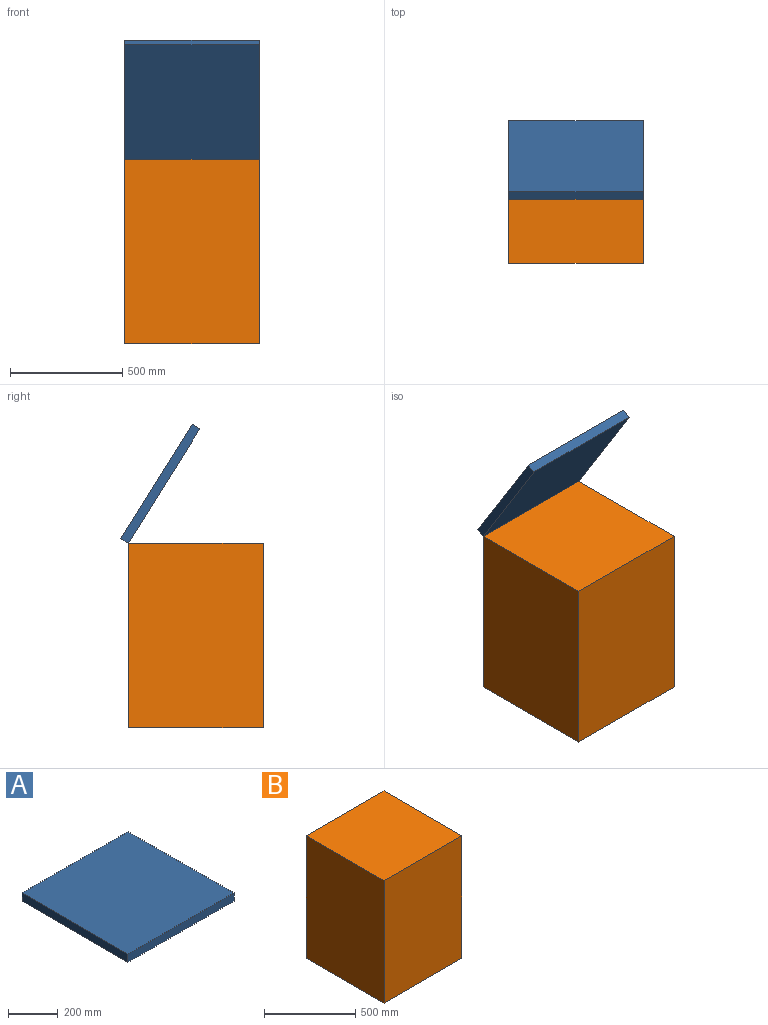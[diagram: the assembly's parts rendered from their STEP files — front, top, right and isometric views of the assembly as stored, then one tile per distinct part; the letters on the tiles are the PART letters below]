
ASSEMBLY  parts=2 mates=1
PART A: 6 faces, bbox 600x600x40 mm
  f0: plane 600x40mm, normal (1,0,0), area 24000mm2, adj f1,f3,f4,f5
  f1: plane 600x40mm, normal (0,1,0), area 24000mm2, adj f0,f2,f4,f5
  f2: plane 600x40mm, normal (-1,0,0), area 24000mm2, adj f1,f3,f4,f5
  f3: plane 600x40mm, normal (0,-1,0), area 24000mm2, adj f0,f2,f4,f5
  f4: plane 600x600mm, normal (0,0,1), area 360000mm2, adj f0,f1,f2,f3
  f5: plane 600x600mm, normal (0,0,-1), area 360000mm2, adj f0,f1,f2,f3
PART B: 6 faces, bbox 600x600x820 mm
  f0: plane 820x600mm, normal (1,0,0), area 492000mm2, adj f1,f3,f4,f5
  f1: plane 820x600mm, normal (0,1,0), area 492000mm2, adj f0,f2,f4,f5
  f2: plane 820x600mm, normal (-1,0,0), area 492000mm2, adj f1,f3,f4,f5
  f3: plane 820x600mm, normal (0,-1,0), area 492000mm2, adj f0,f2,f4,f5
  f4: plane 600x600mm, normal (0,0,-1), area 360000mm2, adj f0,f1,f2,f3
  f5: plane 600x600mm, normal (0,0,1), area 360000mm2, adj f0,f1,f2,f3
PLACE A rot(axis=(-1,0,0),58deg) t=(0,141.02,254.41)mm
PLACE B at identity fixed
MATE revolute A.f0 <-> B.f0  axis (1,0,0) through (300,300,0)mm
